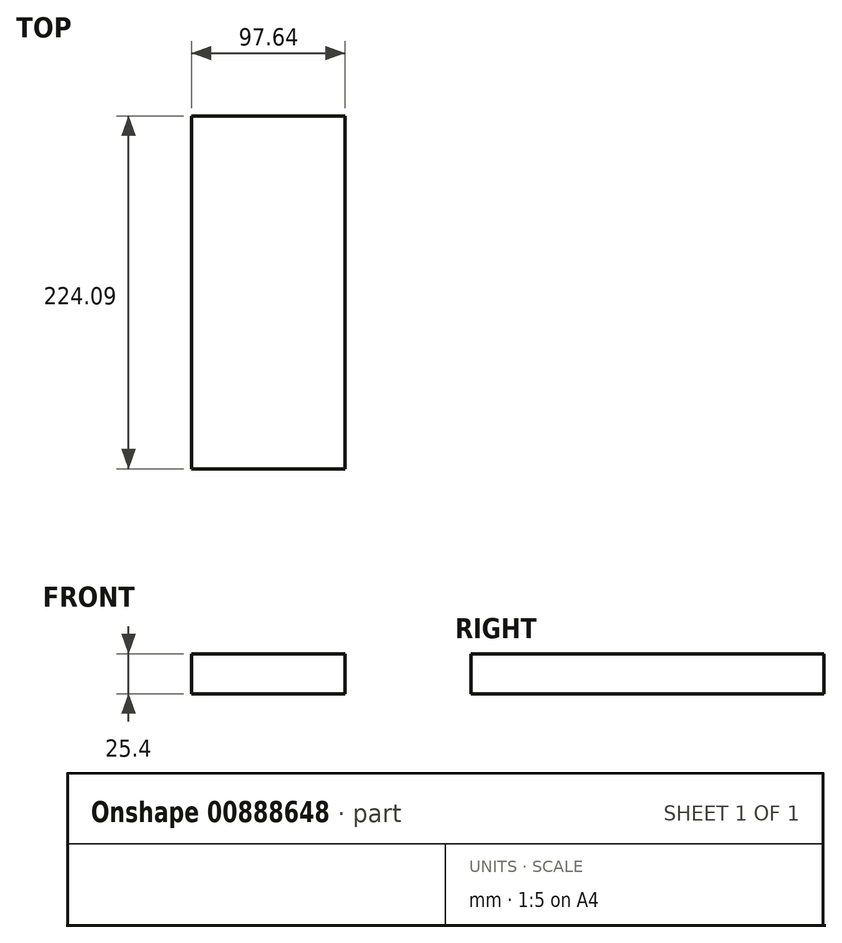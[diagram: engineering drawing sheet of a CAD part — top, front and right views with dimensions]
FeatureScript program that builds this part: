
annotation { "Feature Type Name" : "Feature", "Feature Type Description" : "" }
export const myFeature = defineFeature(function(context is Context, id is Id, definition is map)
    precondition{}
    {
        {
            var Q0;
            Q0=qCreatedBy(makeId("Top.planeOp"),FACE);
            var sketch = newSketch(context, id + "F0", { "sketchPlane" : qUnion([Q0])});
            skLineSegment(sketch, "E0.bottom", {"start": v(-55.46, 122.56) * mm, "end": v(42.18, 122.56) * mm});
            skLineSegment(sketch, "E0.top", {"start": v(-55.46, -101.53) * mm, "end": v(42.18, -101.53) * mm});
            skLineSegment(sketch, "E0.left", {"start": v(-55.46, 122.56) * mm, "end": v(-55.46, -101.53) * mm});
            skLineSegment(sketch, "E0.right", {"start": v(42.18, 122.56) * mm, "end": v(42.18, -101.53) * mm});
            skSolve(sketch);
        }
        {
            var Q0;
            Q0=makeQuery(id+"F0.imprint","IMPRINT",FACE,{"disambiguationData":[TD([[makeQuery(id+"F0.imprint","IMPRINT",EDGE,{"derivedFrom":sQuery(id+"F0.wireOp",EDGE,"E0.bottom")}),-1.0]])]});
            extrude(context, id + "F1", {"entities" : qUnion([Q0]), "depth" : 25.4 * mm, "offsetDistance" : 25.4 * mm});
        }
    });
